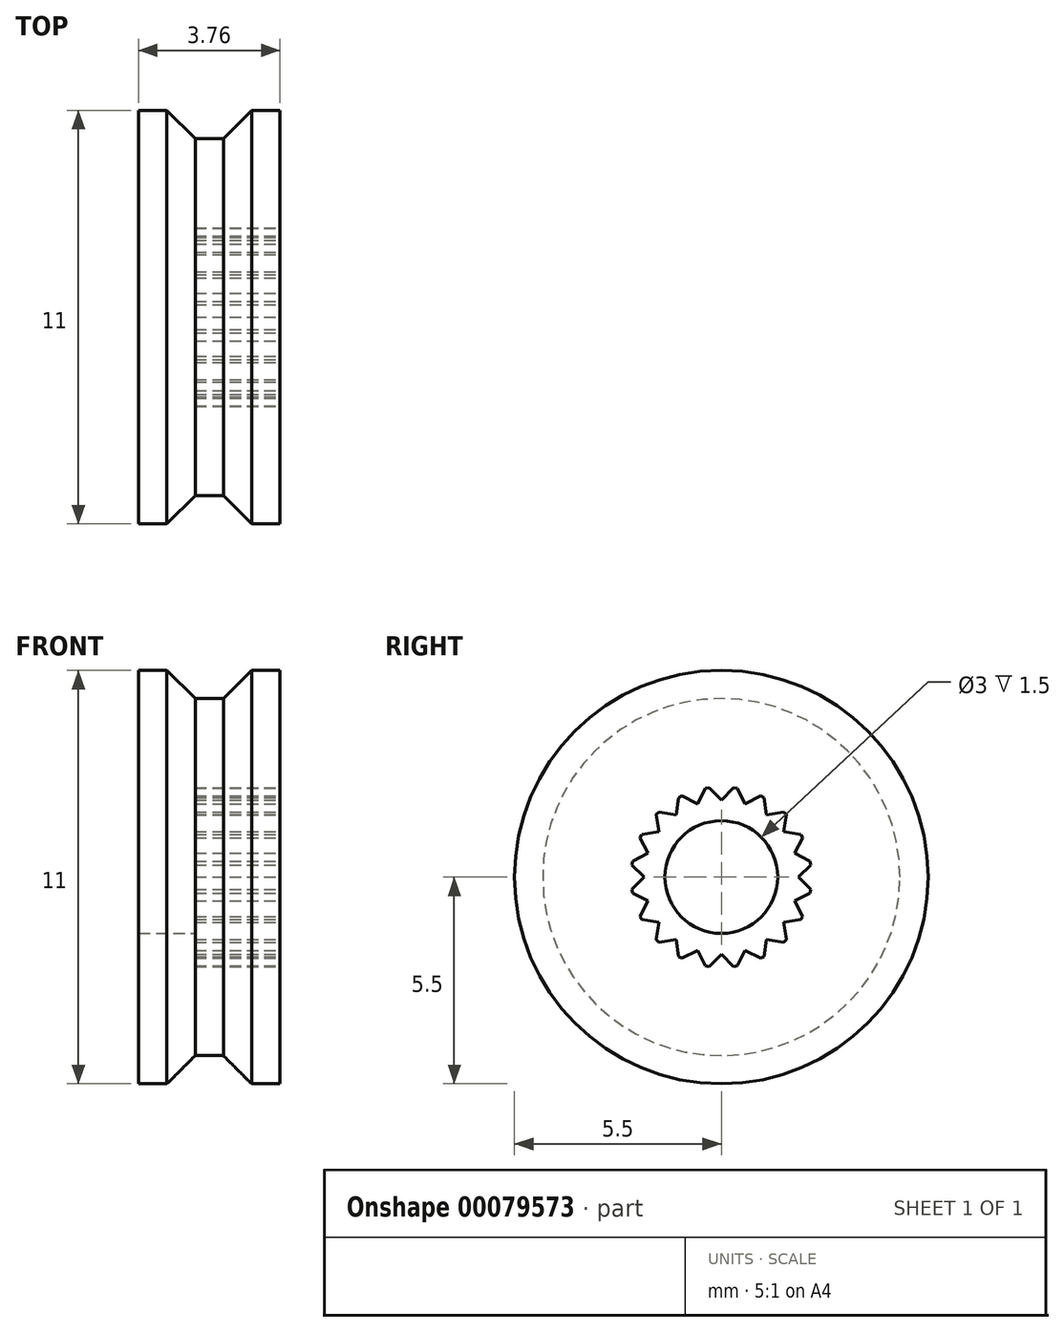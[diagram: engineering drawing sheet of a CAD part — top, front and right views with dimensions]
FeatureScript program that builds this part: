
annotation { "Feature Type Name" : "Feature", "Feature Type Description" : "" }
export const myFeature = defineFeature(function(context is Context, id is Id, definition is map)
    precondition{}
    {
        {
            var Q0;
            Q0=qCreatedBy(makeId("Front.planeOp"),FACE);
            var sketch = newSketch(context, id + "F0", { "sketchPlane" : qUnion([Q0])});
            skLineSegment(sketch, "E0", {"start": v(-1.88, 0) * mm, "end": v(-1.88, 6.25) * mm});
            skLineSegment(sketch, "E1", {"start": v(-1.88, 6.25) * mm, "end": v(-0.38, 4.75) * mm});
            skLineSegment(sketch, "E2", {"start": v(-0.38, 4.75) * mm, "end": v(0.37, 4.75) * mm});
            skLineSegment(sketch, "E3", {"start": v(0.37, 4.75) * mm, "end": v(1.88, 6.25) * mm});
            skLineSegment(sketch, "E4", {"start": v(1.87, 6.25) * mm, "end": v(1.87, 0) * mm});
            skLineSegment(sketch, "E5", {"start": v(1.87, 0) * mm, "end": v(-1.87, 0) * mm});
            skPoint(sketch, "E6", {"position": v(0, 0) * mm});
            skLineSegment(sketch, "E7", {"start": v(-1.88, 5.5) * mm, "end": v(1.87, 5.5) * mm});
            skSolve(sketch);
        }
        {
            var Q0;
            {var subQ10=sQuery(id+"F0.wireOp",EDGE,"E2");Q0=makeQuery(id+"F0.imprint","IMPRINT",FACE,{"disambiguationData":[TD([[makeQuery(id+"F0.imprint","IMPRINT",EDGE,{"derivedFrom":subQ10}),-1.0]])]});}
            var Q1;
            Q1=sQuery(id+"F0.wireOp",EDGE,"E5");
            revolve(context, id + "F1", {"entities" : qUnion([Q0]), "axis" : qUnion([Q1]), "revolveType" : RevolveType.FULL});
        }
        {
            var Q0;
            Q0=makeQuery(id+"F1.opRevolve","SWEPT_FACE",FACE,{"disambiguationData":[OSD([sQuery(id+"F0.wireOp",EDGE,"E4")])]});
            var sketch = newSketch(context, id + "F2", { "sketchPlane" : qUnion([Q0])});
            skLineSegment(sketch, "E8", {"start": v(-1.05, 2.16) * mm, "end": v(-0.63, 1.95) * mm});
            skLineSegment(sketch, "E9", {"start": v(-0.63, 1.95) * mm, "end": v(-0.42, 2.36) * mm});
            skLineSegment(sketch, "E10", {"start": v(-0.42, 2.36) * mm, "end": v(-0.33, 2.38) * mm});
            skLineSegment(sketch, "E11", {"start": v(-0.33, 2.38) * mm, "end": v(0, 2.05) * mm});
            skLineSegment(sketch, "E12", {"start": v(0, 2.05) * mm, "end": v(0.33, 2.38) * mm});
            skLineSegment(sketch, "E13", {"start": v(0.33, 2.38) * mm, "end": v(0.42, 2.36) * mm});
            skLineSegment(sketch, "E14", {"start": v(0.42, 2.36) * mm, "end": v(0.63, 1.95) * mm});
            skLineSegment(sketch, "E15", {"start": v(0.63, 1.95) * mm, "end": v(1.05, 2.16) * mm});
            skLineSegment(sketch, "E16", {"start": v(1.05, 2.16) * mm, "end": v(1.13, 2.12) * mm});
            skLineSegment(sketch, "E17", {"start": v(1.13, 2.12) * mm, "end": v(1.2, 1.66) * mm});
            skLineSegment(sketch, "E18", {"start": v(1.2, 1.66) * mm, "end": v(1.66, 1.73) * mm});
            skLineSegment(sketch, "E19", {"start": v(1.66, 1.73) * mm, "end": v(1.73, 1.66) * mm});
            skLineSegment(sketch, "E20", {"start": v(1.73, 1.66) * mm, "end": v(1.66, 1.2) * mm});
            skLineSegment(sketch, "E21", {"start": v(1.66, 1.2) * mm, "end": v(2.12, 1.13) * mm});
            skLineSegment(sketch, "E22", {"start": v(2.12, 1.13) * mm, "end": v(2.16, 1.05) * mm});
            skLineSegment(sketch, "E23", {"start": v(2.16, 1.05) * mm, "end": v(1.95, 0.63) * mm});
            skLineSegment(sketch, "E24", {"start": v(1.95, 0.63) * mm, "end": v(2.36, 0.42) * mm});
            skLineSegment(sketch, "E25", {"start": v(2.36, 0.42) * mm, "end": v(2.38, 0.33) * mm});
            skLineSegment(sketch, "E26", {"start": v(2.38, 0.33) * mm, "end": v(2.05, 0) * mm});
            skLineSegment(sketch, "E27", {"start": v(2.05, 0) * mm, "end": v(2.38, -0.33) * mm});
            skLineSegment(sketch, "E28", {"start": v(2.38, -0.33) * mm, "end": v(2.36, -0.42) * mm});
            skLineSegment(sketch, "E29", {"start": v(2.36, -0.42) * mm, "end": v(1.95, -0.63) * mm});
            skLineSegment(sketch, "E30", {"start": v(1.95, -0.63) * mm, "end": v(2.16, -1.05) * mm});
            skLineSegment(sketch, "E31", {"start": v(2.16, -1.05) * mm, "end": v(2.12, -1.13) * mm});
            skLineSegment(sketch, "E32", {"start": v(2.12, -1.13) * mm, "end": v(1.66, -1.2) * mm});
            skLineSegment(sketch, "E33", {"start": v(1.66, -1.2) * mm, "end": v(1.73, -1.66) * mm});
            skLineSegment(sketch, "E34", {"start": v(1.73, -1.66) * mm, "end": v(1.66, -1.73) * mm});
            skLineSegment(sketch, "E35", {"start": v(1.66, -1.73) * mm, "end": v(1.2, -1.66) * mm});
            skLineSegment(sketch, "E36", {"start": v(1.2, -1.66) * mm, "end": v(1.13, -2.12) * mm});
            skLineSegment(sketch, "E37", {"start": v(1.13, -2.12) * mm, "end": v(1.05, -2.16) * mm});
            skLineSegment(sketch, "E38", {"start": v(1.05, -2.16) * mm, "end": v(0.63, -1.95) * mm});
            skLineSegment(sketch, "E39", {"start": v(0.63, -1.95) * mm, "end": v(0.42, -2.36) * mm});
            skLineSegment(sketch, "E40", {"start": v(0.42, -2.36) * mm, "end": v(0.33, -2.38) * mm});
            skLineSegment(sketch, "E41", {"start": v(0.33, -2.38) * mm, "end": v(0, -2.05) * mm});
            skLineSegment(sketch, "E42", {"start": v(0, -2.05) * mm, "end": v(-0.33, -2.38) * mm});
            skLineSegment(sketch, "E43", {"start": v(-0.33, -2.38) * mm, "end": v(-0.42, -2.36) * mm});
            skLineSegment(sketch, "E44", {"start": v(-0.42, -2.36) * mm, "end": v(-0.63, -1.95) * mm});
            skLineSegment(sketch, "E45", {"start": v(-0.63, -1.95) * mm, "end": v(-1.05, -2.16) * mm});
            skLineSegment(sketch, "E46", {"start": v(-1.05, -2.16) * mm, "end": v(-1.13, -2.12) * mm});
            skLineSegment(sketch, "E47", {"start": v(-1.13, -2.12) * mm, "end": v(-1.2, -1.66) * mm});
            skLineSegment(sketch, "E48", {"start": v(-1.2, -1.66) * mm, "end": v(-1.66, -1.73) * mm});
            skLineSegment(sketch, "E49", {"start": v(-1.66, -1.73) * mm, "end": v(-1.73, -1.66) * mm});
            skLineSegment(sketch, "E50", {"start": v(-1.73, -1.66) * mm, "end": v(-1.66, -1.2) * mm});
            skLineSegment(sketch, "E51", {"start": v(-1.66, -1.2) * mm, "end": v(-2.12, -1.13) * mm});
            skLineSegment(sketch, "E52", {"start": v(-2.12, -1.13) * mm, "end": v(-2.16, -1.05) * mm});
            skLineSegment(sketch, "E53", {"start": v(-2.16, -1.05) * mm, "end": v(-1.95, -0.63) * mm});
            skLineSegment(sketch, "E54", {"start": v(-1.95, -0.63) * mm, "end": v(-2.36, -0.42) * mm});
            skLineSegment(sketch, "E55", {"start": v(-2.36, -0.42) * mm, "end": v(-2.38, -0.33) * mm});
            skLineSegment(sketch, "E56", {"start": v(-2.38, -0.33) * mm, "end": v(-2.05, 0) * mm});
            skLineSegment(sketch, "E57", {"start": v(-2.05, 0) * mm, "end": v(-2.38, 0.33) * mm});
            skLineSegment(sketch, "E58", {"start": v(-2.38, 0.33) * mm, "end": v(-2.36, 0.42) * mm});
            skLineSegment(sketch, "E59", {"start": v(-2.36, 0.42) * mm, "end": v(-1.95, 0.63) * mm});
            skLineSegment(sketch, "E60", {"start": v(-1.95, 0.63) * mm, "end": v(-2.16, 1.05) * mm});
            skLineSegment(sketch, "E61", {"start": v(-2.16, 1.05) * mm, "end": v(-2.12, 1.13) * mm});
            skLineSegment(sketch, "E62", {"start": v(-2.12, 1.13) * mm, "end": v(-1.66, 1.2) * mm});
            skLineSegment(sketch, "E63", {"start": v(-1.66, 1.2) * mm, "end": v(-1.73, 1.66) * mm});
            skLineSegment(sketch, "E64", {"start": v(-1.73, 1.66) * mm, "end": v(-1.66, 1.73) * mm});
            skLineSegment(sketch, "E65", {"start": v(-1.66, 1.73) * mm, "end": v(-1.2, 1.66) * mm});
            skLineSegment(sketch, "E66", {"start": v(-1.2, 1.66) * mm, "end": v(-1.13, 2.12) * mm});
            skLineSegment(sketch, "E67", {"start": v(-1.13, 2.12) * mm, "end": v(-1.05, 2.16) * mm});
            skPoint(sketch, "E68", {"position": v(0, 0) * mm});
            skCircle(sketch, "E69", {"center": v(0, 0) * mm, "radius": 2.05 * mm, "construction": true});
            skCircle(sketch, "E70", {"center": v(0, 0) * mm, "radius": 2.4 * mm, "construction": true});
            skCircle(sketch, "E71", {"center": v(0, 0) * mm, "radius": 1.5 * mm});
            skSolve(sketch);
        }
        {
            var Q0;
            Q0=makeQuery(id+"F2.imprint","IMPRINT",FACE,{"disambiguationData":[TD([[makeQuery(id+"F2.imprint","IMPRINT",EDGE,{"derivedFrom":sQuery(id+"F2.wireOp",EDGE,"E8")}),-1.0]])]});
            extrude(context, id + "F3", {"entities" : qUnion([Q0]), "operationType" : NewBodyOperationType.REMOVE, "oppositeDirection" : true, "depth" : 2.25 * mm});
        }
        {
            var Q0;
            Q0=makeQuery(id+"F2.imprint","IMPRINT",FACE,{"disambiguationData":[TD([[makeQuery(id+"F2.imprint","IMPRINT",EDGE,{"derivedFrom":sQuery(id+"F2.wireOp",EDGE,"E71")}),1.0]])]});
            extrude(context, id + "F4", {"entities" : qUnion([Q0]), "operationType" : NewBodyOperationType.REMOVE, "endBound" : BoundingType.THROUGH_ALL, "oppositeDirection" : true, "depth" : 25 * mm});
        }
    });
